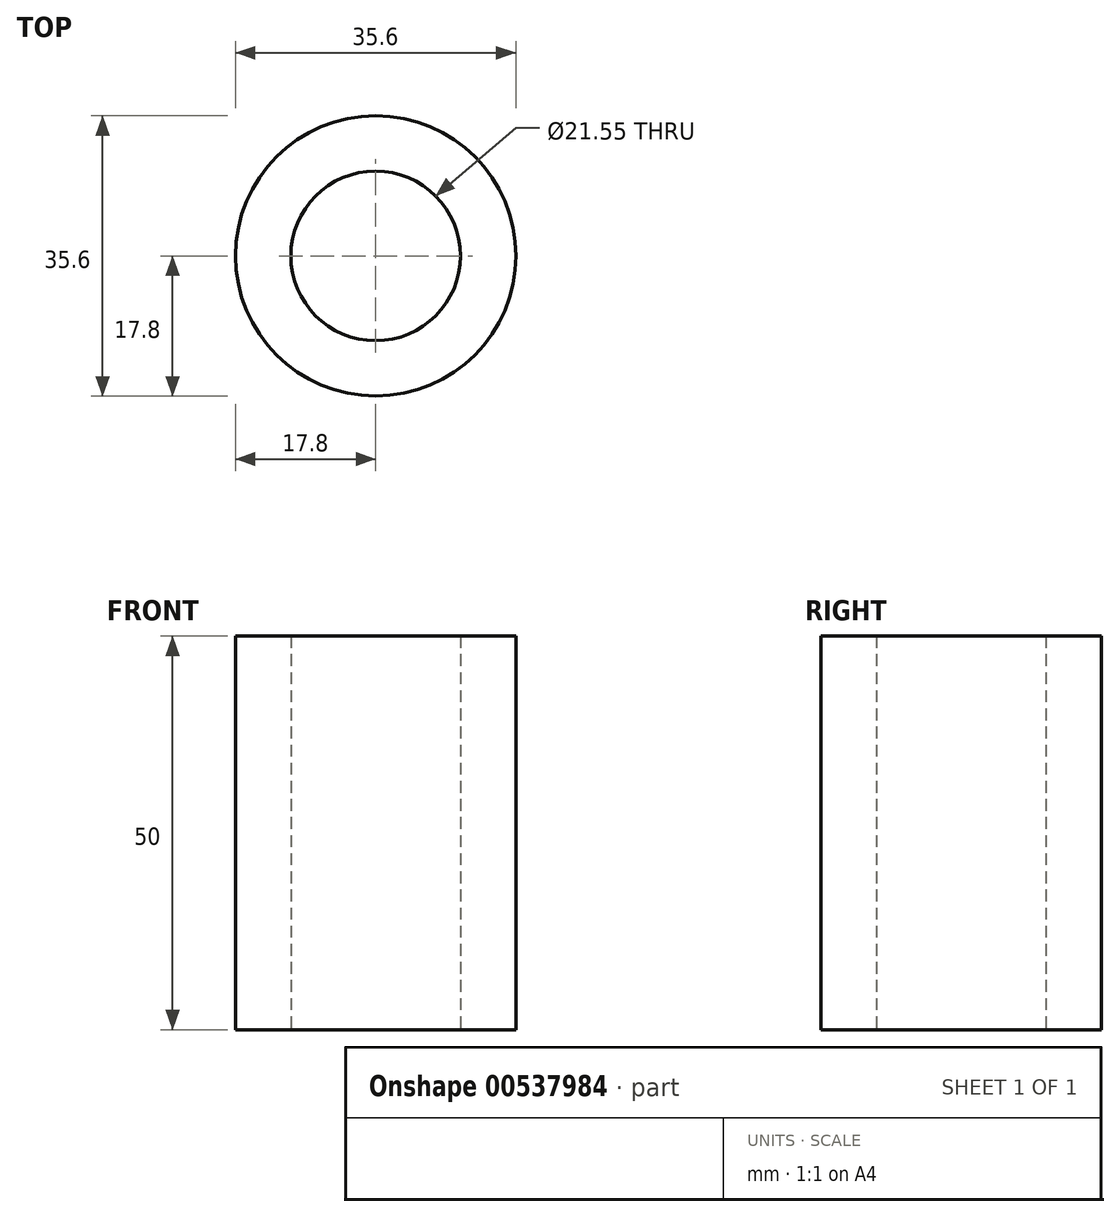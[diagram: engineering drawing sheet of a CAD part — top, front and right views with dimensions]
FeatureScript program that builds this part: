
annotation { "Feature Type Name" : "Feature", "Feature Type Description" : "" }
export const myFeature = defineFeature(function(context is Context, id is Id, definition is map)
    precondition{}
    {
        {
            var Q0;
            Q0=qCreatedBy(makeId("Top.planeOp"),FACE);
            var sketch = newSketch(context, id + "F0", { "sketchPlane" : qUnion([Q0])});
            skCircle(sketch, "E0", {"center": v(0, 0) * mm, "radius": 10.77 * mm});
            skCircle(sketch, "E1", {"center": v(0, 0) * mm, "radius": 17.8 * mm});
            skSolve(sketch);
        }
        {
            var Q0;
            Q0=makeQuery(id+"F0.imprint","IMPRINT",FACE,{"disambiguationData":[TD([[makeQuery(id+"F0.imprint","IMPRINT",EDGE,{"derivedFrom":sQuery(id+"F0.wireOp",EDGE,"E0")}),-1.0]])]});
            extrude(context, id + "F1", {"entities" : qUnion([Q0]), "depth" : 50 * mm, "offsetDistance" : 25 * mm});
        }
    });
